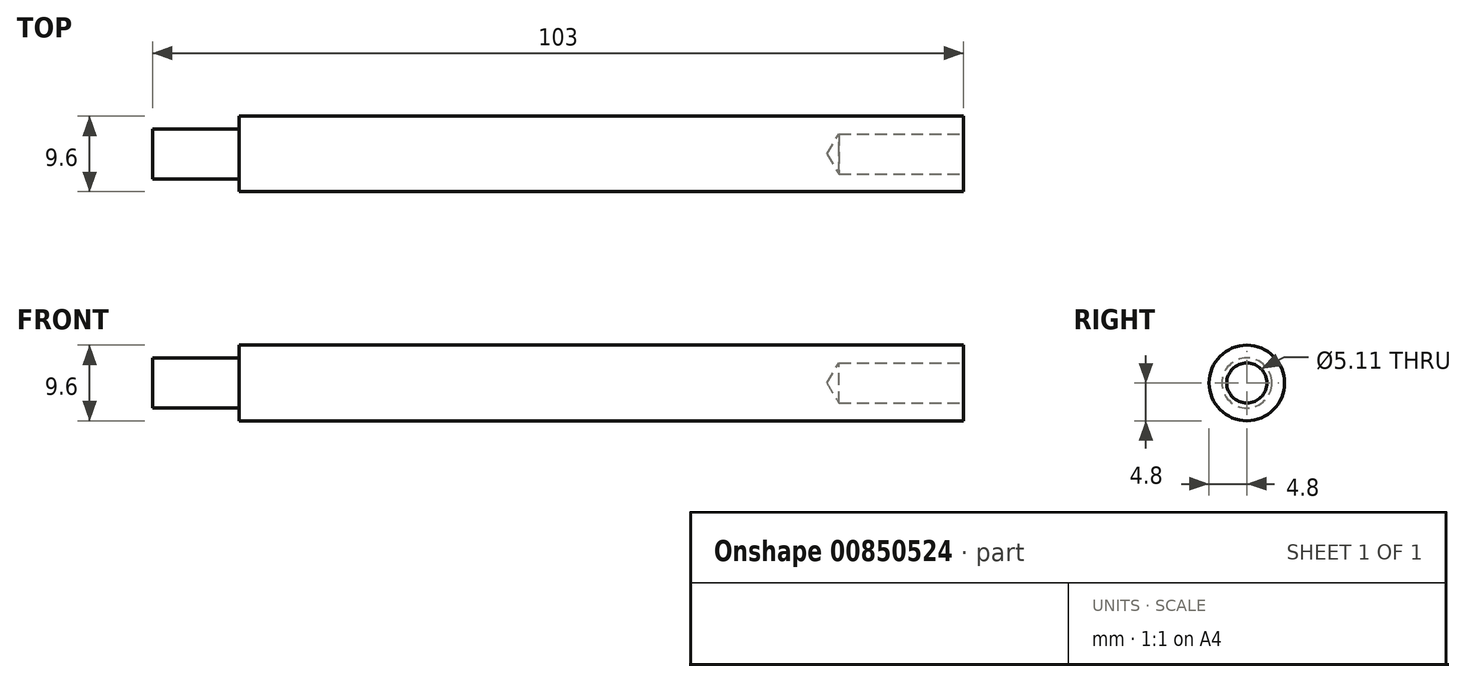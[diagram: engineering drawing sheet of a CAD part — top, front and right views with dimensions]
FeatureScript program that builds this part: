
annotation { "Feature Type Name" : "Feature", "Feature Type Description" : "" }
export const myFeature = defineFeature(function(context is Context, id is Id, definition is map)
    precondition{}
    {
        {
            var Q0;
            Q0=qCreatedBy(makeId("Right.planeOp"),FACE);
            var sketch = newSketch(context, id + "F0", { "sketchPlane" : qUnion([Q0])});
            skCircle(sketch, "E0", {"center": v(0, 0) * mm, "radius": 4.8 * mm});
            skSolve(sketch);
        }
        {
            var Q0;
            Q0=qSketchRegion(id+"F0",true);
            extrude(context, id + "F1", {"entities" : qUnion([Q0]), "endBound" : BoundingType.SYMMETRIC, "depth" : 92 * mm, "offsetDistance" : 25 * mm});
        }
        {
            var Q0;
            Q0=makeQuery(id+"F1.opExtrude","CAP_FACE",FACE,{"disambiguationData":[OSD([sQuery(id+"F0.wireOp",EDGE,"E0")])],"isStart":false});
            var sketch = newSketch(context, id + "F2", { "sketchPlane" : qUnion([Q0])});
            skPoint(sketch, "E1", {"position": v(0, 0) * mm});
            skSolve(sketch);
        }
        {
            var Q0;
            Q0=sQuery(id+"F2.wireOp",VERTEX,"E1");
            var Q1;
            Q1=makeQuery(id+"F1.opExtrude","SWEPT_BODY",BODY,{"disambiguationData":[OSD([sQuery(id+"F0.wireOp",EDGE,"E0")])]});
            hole(context, id + "F3", {"style" : HoleStyle.SIMPLE, "endStyle" : HoleEndStyle.BLIND, "standardTappedOrClearance" : lookupTablePath({ "standard" : "ANSI", "engagement" : "75%", "pitch" : "20 tpi", "size" : "1/4", "type" : "Tapped" }), "standardBlindInLast" : lookupTablePath({ "standard" : "ANSI", "engagement" : "75%", "pitch" : "20 tpi", "size" : "1/4", "type" : "Tapped" }), "holeDiameter" : 5.1 * mm, "majorDiameter" : 6.35 * mm, "showTappedDepth" : true, "holeDepth" : 15.8 * mm, "isTappedThrough" : true, "tappedDepth" : 12 * mm, "tapClearance" : 3, "locations" : qUnion([Q0]), "scope" : qUnion([Q1])});
        }
        {
            var Q0;
            Q0=makeQuery(id+"F1.opExtrude","CAP_FACE",FACE,{"disambiguationData":[OSD([sQuery(id+"F0.wireOp",EDGE,"E0")])],"isStart":true});
            var sketch = newSketch(context, id + "F4", { "sketchPlane" : qUnion([Q0])});
            skCircle(sketch, "E2", {"center": v(0, 0) * mm, "radius": 3.17 * mm});
            skSolve(sketch);
        }
        {
            var Q0;
            Q0=qSketchRegion(id+"F4",true);
            extrude(context, id + "F5", {"entities" : qUnion([Q0]), "operationType" : NewBodyOperationType.ADD, "depth" : 11 * mm, "offsetDistance" : 25 * mm});
        }
    });
